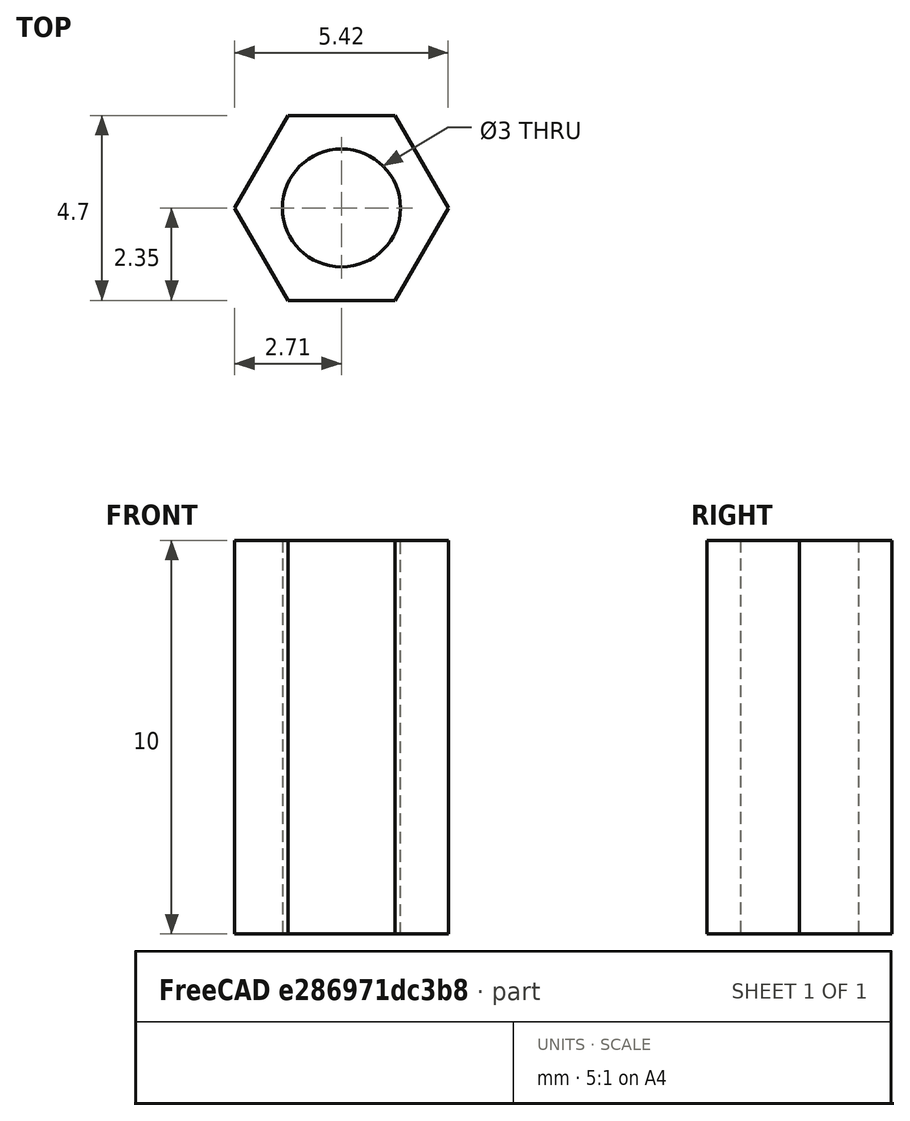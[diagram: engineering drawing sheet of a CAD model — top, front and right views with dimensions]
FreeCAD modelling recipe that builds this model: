
FCSTD DOCUMENT  (FreeCAD 0.18.4R)
Label: coxial_M3_10mm
License: All rights reserved
LicenseURL: http://en.wikipedia.org/wiki/All_rights_reserved
objects: Sketcher::SketchObject×1, PartDesign::Pad×1, PartDesign::Body×1
note: 4 computed .brp shape members not serialized (recipe doc carries the construction recipe); baked Part::Feature solids carry a one-line shape summary decoded from their .brp

FEATURE [Sketcher::SketchObject] Sketch
  MapMode = 5
  Support = -> [XY_Plane]
  sketch-geometry (8):
    g0: Circle CenterX=0 CenterY=0 CenterZ=0 NormalX=0 NormalY=0 NormalZ=1 AngleXU=0 Radius=1.5
    g1: LineSegment StartX=1.35677 StartY=-2.35 StartZ=0 EndX=2.71355 EndY=-4e-16 EndZ=0
    g2: LineSegment StartX=2.71355 StartY=-6e-16 StartZ=0 EndX=1.35677 EndY=2.35 EndZ=0
    g3: LineSegment StartX=1.35677 StartY=2.35 StartZ=0 EndX=-1.35677 EndY=2.35 EndZ=0
    g4: LineSegment StartX=-1.35677 StartY=2.35 StartZ=0 EndX=-2.71355 EndY=1.3e-15 EndZ=0
    g5: LineSegment StartX=-2.71355 StartY=1.3e-15 StartZ=0 EndX=-1.35677 EndY=-2.35 EndZ=0
    g6: LineSegment StartX=-1.35677 StartY=-2.35 StartZ=0 EndX=1.35677 EndY=-2.35 EndZ=0
    g7: Circle [constr] CenterX=0 CenterY=0 CenterZ=0 NormalX=0 NormalY=0 NormalZ=1 AngleXU=0 Radius=2.71355
  constraints (18):
    c: Coincident(g0,g-1)
    c: Radius(g0) = 1.5
    c: Coincident(g1,g2)
    c: Coincident(g2,g3)
    c: Coincident(g3,g4)
    c: Coincident(g4,g5)
    c: Coincident(g5,g6)
    c: Coincident(g6,g1)
    c: Equal(g1, g2-g6) x5
    c: PointOnObject(g1,g7)
    c: PointOnObject(g2,g7)
    c: PointOnObject(g3,g7)
    c: PointOnObject(g4,g7)
    c: PointOnObject(g5,g7)
    c: PointOnObject(g6,g7)
    c: Distance(g2,g4) = 4.7
    c: Coincident(g7,g0)
    c: Horizontal(g3)
FEATURE [PartDesign::Pad] Pad
  Length = 10
  Length2 = 100
  Profile = -> Sketch
  Type = 0
FEATURE [PartDesign::Body] Body
  Group = -> [Sketch,Pad]
  Origin = -> Origin
  Tip = -> Pad
